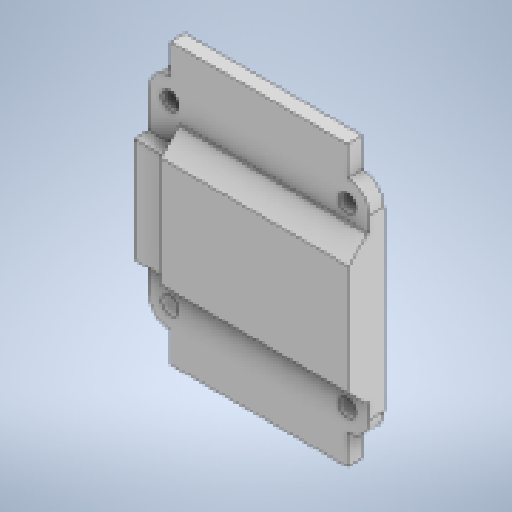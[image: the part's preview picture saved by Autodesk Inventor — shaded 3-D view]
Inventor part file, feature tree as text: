
AUTODESK INVENTOR PART (.ipt)
format: ipt  version: 2023 (Build 270158000, 158)  size: 233,984 bytes
history: native  units: in
note: dims shown in document units (in); Inventor stores cm internally (conversion verified against a paired STEP export)
features: extrude x5, sketch x5, other x3, chamfer x2, projected_geometry x2, reference x1
ambient origin geometry x8: Origin, YZ Plane, XZ Plane, XY Plane, X Axis, Y Axis, Z Axis, Center Point
bodies: Solid1 (feature_tree)
feature tree (18):
  extrude  "Extrusion1"  Depth=0.1476in
  extrude  "Extrusion2"  Depth=0.1in TaperAngle=0.0deg
  extrude  "Extrusion3"  Depth=0.3935in
  chamfer  "Chamfer1"  Distance=0.1in
  chamfer  "Chamfer2"  Distance=0.25in
  extrude  "Extrusion4"  Depth=0.14in TaperAngle=0.0deg
  extrude  "Extrusion5"  Depth=0.2in TaperAngle=45.0deg
  sketch  "Sketch1"  dims[d0=0.1476in d1=0.1476in]
  reference  "Reference1"
  sketch  "Sketch2"  dims[d2=0.1476in d3=0.1in d4=0.0in]
  sketch  "Sketch3"  dims[d5=0.3935in d6=0.3935in]
  sketch  "Sketch4"  dims[d7=0.2in d8=0.1in d9=0.0in]
  projected_geometry  "Projected Loop1"
  sketch  "Sketch5"  dims[d10=0.25in d11=0.25in d12=0.14in d13=0.0in d14=0.125in d15=0.125in d16=45.0deg d17=0.125in d18=0.125in d19=45.0deg d20=0.2in d21=0.0in d22=0.2in d23=0.0in]
  projected_geometry  "Projected Loop2"
  parser-record x1  (decoder bookkeeping rows leaked as tree rows — omitted from the tree; the rows remain in map.json)
  other  "ECE477.iam"
  other  "Source Two v0.1_import:1"
note: 1 file-system path scrubbed to <path> (originals preserved in map.json)
